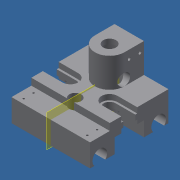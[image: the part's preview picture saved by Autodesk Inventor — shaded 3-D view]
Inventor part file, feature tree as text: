
AUTODESK INVENTOR PART (.ipt)
format: ipt  version: 2018 (Build 220112000, 112)  size: 335,360 bytes
history: native  units: mm
features: extrude x14, sketch x14, plane x2, mirror x2, other x1
ambient origin geometry x8: Origin, YZ Plane, XZ Plane, XY Plane, X Axis, Y Axis, Z Axis, Center Point
bodies: Solid1 (feature_tree)
feature tree (33):
  other  "<userpath>\OneDrive\Objet3D\3DPrinter\Parameters.xlsx"
  extrude  "Extrusion1"  Depth=80.0mm
  extrude  "Extrusion2"  Depth=40.0mm
  extrude  "Extrusion3"  Depth=12.2mm
  extrude  "Extrusion4"  Depth=10.0mm
  extrude  "Extrusion5"  Depth=5.5mm TaperAngle=0.0deg
  extrude  "Extrusion6"  Depth=4.0mm TaperAngle=0.0deg
  plane  "Work Plane1"
  mirror  "Mirror1"
  extrude  "Extrusion8"  Depth=8.1mm
  extrude  "Extrusion9"  Depth=25.0mm
  plane  "Work Plane2"
  mirror  "Mirror2"
  extrude  "Extrusion10"  Depth=15.0mm
  extrude  "Extrusion11"  Depth=5.0mm
  extrude  "Extrusion12"  Depth=5.0mm
  extrude  "Extrusion13"  Depth=0.0mm
  extrude  "Extrusion14"  Depth=15.0mm
  extrude  "Extrusion15"  Depth=10.0mm
  sketch  "Sketch1"  dims[d0=80.0mm d1=80.0mm]
  sketch  "Sketch2"  dims[d2=15.0mm d3=0.0mm d7=40.0mm]
  sketch  "Sketch3"  dims[d8=20.0mm d9=12.2mm]
  sketch  "Sketch4"  dims[d10=10.0mm d11=0.0mm d12=16.2mm]
  sketch  "Sketch5"  dims[d13=4.0mm d14=0.0mm d15=5.5mm d16=0.0mm]
  sketch  "Sketch6"  dims[d17=13.8mm d18=4.0mm d19=0.0mm]
  sketch  "Sketch8"  dims[d20=16.2mm d21=8.1mm]
  sketch  "Sketch9"  dims[d22=25.0mm d23=25.0mm]
  sketch  "Sketch10"  dims[d24=15.0mm d25=15.0mm]
  sketch  "Sketch11"  dims[d29=15.0mm d30=5.0mm d31=5.0mm d32=15.0mm]
  sketch  "Sketch12"  dims[d33=5.0mm d34=5.0mm]
  sketch  "Sketch13"  dims[d35=80.0mm d36=0.0mm d37=0.0mm]
  sketch  "Sketch14"  dims[d38=15.0mm d39=15.0mm]
  sketch  "Sketch15"  dims[d40=60.0mm d41=10.0mm d42=10.0mm d49=20.2mm d50=7.0mm d51=0.0mm d52=0.0mm d53=1.9mm d54=1.9mm d55=7.6mm d56=7.6mm d57=10.0mm d58=4.9mm d59=10.0mm d60=0.0mm d61=12.0mm d62=20.0mm d63=0.0mm d64=30.0mm d65=20.0mm d66=40.0mm d67=20.0mm d68=30.0mm d69=0.0mm d70=13.0mm d71=5.0mm d72=0.0mm d73=35.0mm d74=0.0mm d75=2.9mm d76=2.9mm d77=11.0mm d78=4.0mm d79=8.5mm d80=8.5mm d81=15.0mm d82=0.0mm d83=6.0mm d84=15.0mm d85=8.0mm d86=17.0mm d87=0.0mm]
